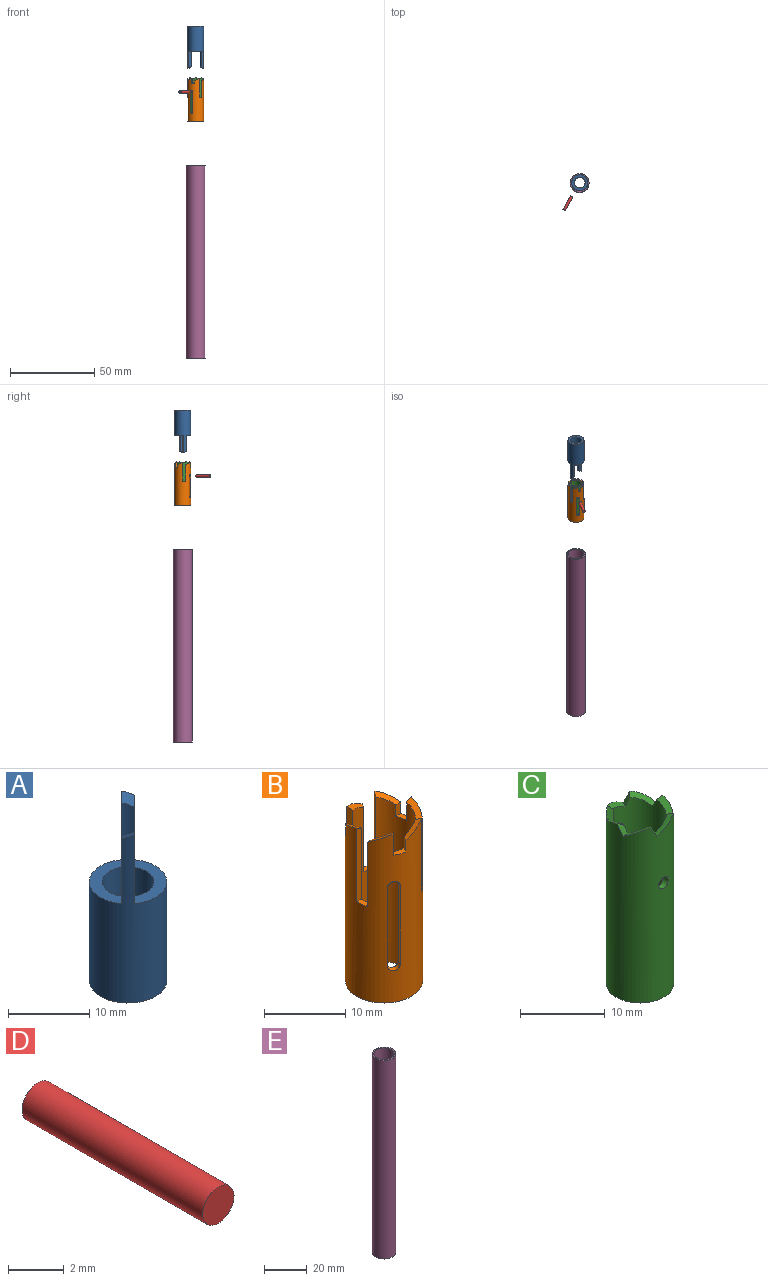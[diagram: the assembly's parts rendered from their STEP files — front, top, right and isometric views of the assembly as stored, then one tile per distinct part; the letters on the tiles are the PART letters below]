
ASSEMBLY  parts=5 mates=4
PART A: 11 faces, bbox 9.5x9.5x25.3 mm
  f0: cylinder r=4.76mm len=25.28mm, axis (0,0,-1), area 477.4mm2, adj f2,f3,f4,f5,f6,f7,f8,f9
  f1: cylinder r=3.17mm len=24.62mm, axis (0,0,-1), area 326.7mm2, adj f2,f3,f4,f5,f6,f7,f8,f9
  f2: plane 2.22x2.22mm, normal (0,0.5,0.87), area 2.8mm2, adj f0,f1,f6,f9
  f3: plane 2.22x2.22mm, normal (0,-0.5,0.87), area 2.8mm2, adj f0,f1,f7,f10
  f4: plane 9.53x9.53mm, normal (0,0,-1), area 39.6mm2, adj f0,f1
  f5: plane 7.55x7.55mm, normal (0,0,1), area 17.4mm2, adj f0,f1,f6,f7
  f6: plane 9.74x1.14mm, normal (-0.71,0.71,0), area 15.2mm2, adj f0,f1,f2,f5
  f7: plane 10.36x1.14mm, normal (-0.71,0.71,0), area 16.2mm2, adj f0,f1,f3,f5
  f8: plane 7.55x7.55mm, normal (0,0,1), area 17.4mm2, adj f0,f1,f9,f10
  f9: plane 10.36x1.14mm, normal (0.71,-0.71,0), area 16.2mm2, adj f0,f1,f2,f8
  f10: plane 9.74x1.14mm, normal (0.71,-0.71,0), area 15.2mm2, adj f0,f1,f3,f8
PART B: 37 faces, bbox 9.5x9.5x25.4 mm
  f0: plane 0.12x0.07mm, normal (0,0,1), area 0mm2, adj f1,f7,f31
  f1: plane 3.18x0.79mm, normal (0,1,0), area 2.4mm2, adj f0,f7,f9,f10,f31
  f2: plane 0.12x0.1mm, normal (0,0,1), area 0mm2, adj f7,f28,f32
  f3: plane 0.12x0.07mm, normal (0,0,1), area 0mm2, adj f7,f17,f24
  f4: plane 0.14x0.06mm, normal (0,0,1), area 0mm2, adj f7,f21,f27
  f5: plane 0.12x0.1mm, normal (0,0,1), area 0mm2, adj f7,f13,f20
  f6: plane 0.14x0.06mm, normal (0,0,1), area 0mm2, adj f7,f12,f16
  f7: cylinder r=4.76mm len=25.4mm, axis (0,0,-1), area 656.2mm2, adj f0,f1,f2,f3,f4,f5,f6,f8
  f8: plane 9.53x9.53mm, normal (0,0,-1), area 21.8mm2, adj f7,f9
  f9: cylinder r=3.97mm len=25.04mm, axis (0,0,-1), area 528.7mm2, adj f1,f8,f10,f11,f12,f13,f14,f15
  f10: plane 1.6x1.13mm, normal (0,0,1), area 1.3mm2, adj f1,f7,f9,f11
  f11: plane 1.75x0.85mm, normal (0,-1,0), area 1.5mm2, adj f7,f9,f10,f12
  f12: plane 2.5x2.46mm, normal (0,-0.5,0.87), area 2.7mm2, adj f6,f7,f9,f11,f16
  f13: plane 3.2x1.42mm, normal (0.43,-0.25,0.87), area 2.7mm2, adj f5,f7,f9,f15,f20
  f14: plane 1.95x1.25mm, normal (0,0,1), area 1.3mm2, adj f7,f9,f15,f16
  f15: plane 9.69x0.74mm, normal (0.87,-0.5,0), area 8.3mm2, adj f7,f9,f13,f14
  f16: plane 11.11x0.69mm, normal (-0.87,0.5,0), area 8.7mm2, adj f6,f7,f9,f12,f14
  f17: plane 3.08x1.56mm, normal (0.43,0.25,0.87), area 2.7mm2, adj f3,f7,f9,f19,f24
  f18: plane 1.78x1.64mm, normal (0,0,1), area 1.3mm2, adj f7,f9,f19,f20
  f19: plane 1.75x0.74mm, normal (0.87,0.5,0), area 1.5mm2, adj f7,f9,f17,f18
  f20: plane 3.18x0.69mm, normal (-0.87,-0.5,0), area 2.4mm2, adj f5,f7,f9,f13,f18
  f21: plane 2.5x2.46mm, normal (0,0.5,0.87), area 2.7mm2, adj f4,f7,f9,f22,f27
  f22: plane 9.68x0.85mm, normal (0,1,0), area 8.3mm2, adj f7,f9,f21,f23
  f23: plane 1.6x1.13mm, normal (0,0,1), area 1.3mm2, adj f7,f9,f22,f24
  f24: plane 11.1x0.79mm, normal (0,-1,0), area 8.7mm2, adj f3,f7,f9,f17,f23
  f25: plane 1.95x1.25mm, normal (0,0,1), area 1.3mm2, adj f7,f9,f26,f27
  f26: plane 1.75x0.74mm, normal (-0.87,0.5,0), area 1.5mm2, adj f7,f9,f25,f28
  f27: plane 3.18x0.69mm, normal (0.87,-0.5,0), area 2.4mm2, adj f4,f7,f9,f21,f25
  f28: plane 3.2x1.42mm, normal (-0.43,0.25,0.87), area 2.7mm2, adj f2,f7,f9,f26,f32
  f29: plane 1.78x1.64mm, normal (0,0,1), area 1.3mm2, adj f7,f9,f30,f32
  f30: plane 9.68x0.74mm, normal (-0.87,-0.5,0), area 8.3mm2, adj f7,f9,f29,f31
  f31: plane 3.08x1.56mm, normal (-0.43,-0.25,0.87), area 2.7mm2, adj f0,f1,f7,f9,f30
  f32: plane 11.1x0.69mm, normal (0.87,0.5,0), area 8.7mm2, adj f2,f7,f9,f28,f29
  f33: cylinder r=0.81mm len=1.85mm, axis (-0.5,-0.87,0), area 2mm2, adj f7,f9,f34,f36
  f34: plane 11.84x0.7mm, normal (0.87,-0.5,0), area 9.6mm2, adj f7,f9,f33,f35
  f35: cylinder r=0.81mm len=1.85mm, axis (-0.5,-0.87,0), area 2mm2, adj f7,f9,f34,f36
  f36: plane 11.84x0.7mm, normal (-0.87,0.5,0), area 9.6mm2, adj f7,f9,f33,f35
PART C: 17 faces, bbox 7.9x7.9x25.1 mm
  f0: cylinder r=3.96mm len=25.09mm, axis (0,0,-1), area 604.2mm2, adj f2,f3,f4,f5,f6,f7,f8,f9
  f1: cylinder r=3.17mm len=24.74mm, axis (0,0,-1), area 479.7mm2, adj f2,f3,f4,f5,f6,f7,f8,f9
  f2: plane 1.46x0.96mm, normal (0,0.87,0.5), area 1.2mm2, adj f0,f1,f7,f13
  f3: plane 3.17x1.45mm, normal (-0.43,0.25,0.87), area 2.7mm2, adj f0,f1,f12,f14
  f4: plane 2.58x2.5mm, normal (0,0.5,0.87), area 2.7mm2, adj f0,f1,f11,f12
  f5: plane 3.2x1.58mm, normal (0.43,0.25,0.87), area 2.7mm2, adj f0,f1,f10,f11
  f6: plane 7.92x7.92mm, normal (0,0,-1), area 17.7mm2, adj f0,f1
  f7: plane 2.58x2.5mm, normal (0,-0.5,0.87), area 2.7mm2, adj f0,f1,f2,f9
  f8: plane 3.17x1.45mm, normal (0.43,-0.25,0.87), area 2.7mm2, adj f0,f1,f9,f10
  f9: plane 1.46x1.21mm, normal (-0.75,0.43,0.5), area 1.2mm2, adj f0,f1,f7,f8
  f10: plane 1.46x1.25mm, normal (-0.75,-0.43,0.5), area 1.2mm2, adj f0,f1,f5,f8
  f11: plane 1.46x0.96mm, normal (0,-0.87,0.5), area 1.2mm2, adj f0,f1,f4,f5
  f12: plane 1.46x1.21mm, normal (0.75,-0.43,0.5), area 1.2mm2, adj f0,f1,f3,f4
  f13: plane 3.19x1.58mm, normal (-0.43,-0.25,0.87), area 2.7mm2, adj f0,f1,f2,f14
  f14: plane 1.46x1.25mm, normal (0.75,0.43,0.5), area 1.2mm2, adj f0,f1,f3,f13
  f15: cylinder r=0.79mm len=1.59mm, axis (0,-1,0), area 4mm2, adj f0,f1
  f16: cylinder r=0.79mm len=1.59mm, axis (0,-1,0), area 4mm2, adj f0,f1
PART D: 3 faces, bbox 1.6x9.1x1.6 mm
  f0: cylinder r=0.79mm len=9.14mm, axis (0,1,0), area 45.6mm2, adj f1,f2
  f1: plane 1.59x1.59mm, normal (0,-1,0), area 2mm2, adj f0
  f2: plane 1.59x1.59mm, normal (0,1,0), area 2mm2, adj f0
PART E: 4 faces, bbox 11.1x11.1x114.3 mm
  f0: cylinder r=4.76mm len=114.3mm, axis (0,0,-1), area 3420.3mm2, adj f2,f3
  f1: cylinder r=5.56mm len=114.3mm, axis (0,0,-1), area 3990.3mm2, adj f2,f3
  f2: plane 11.11x11.11mm, normal (0,0,1), area 25.7mm2, adj f0,f1
  f3: plane 11.11x11.11mm, normal (0,0,-1), area 25.7mm2, adj f0,f1
PLACE A rot(axis=(0.87,0.5,0),180deg) t=(-41.7,68.3,-62.69)mm
PLACE B t=(-41.7,68.3,-119.22)mm
PLACE C rot(axis=(0,0,1),150deg) t=(-41.7,68.3,-118.42)mm
PLACE D rot(axis=(0.26,0.97,0),180deg) t=(-46.4,60.15,-101.91)mm
PLACE E rot(axis=(0,0,1),60deg) t=(-41.7,68.3,-259.83)mm
MATE cylindrical E.f0 <-> C.f0  axis (0,0,-1) through (-41.7,68.3,-202.68)mm
MATE cylindrical D.f0 <-> C.f15  axis (0.5,0.87,0) through (-48.69,56.2,-101.91)mm
MATE cylindrical A.f1 <-> C.f1  axis (0,0,1) through (-41.7,68.3,-75.07)mm
MATE cylindrical B.f9 <-> C.f0  axis (0,0,-1) through (-41.7,68.3,-106.63)mm
